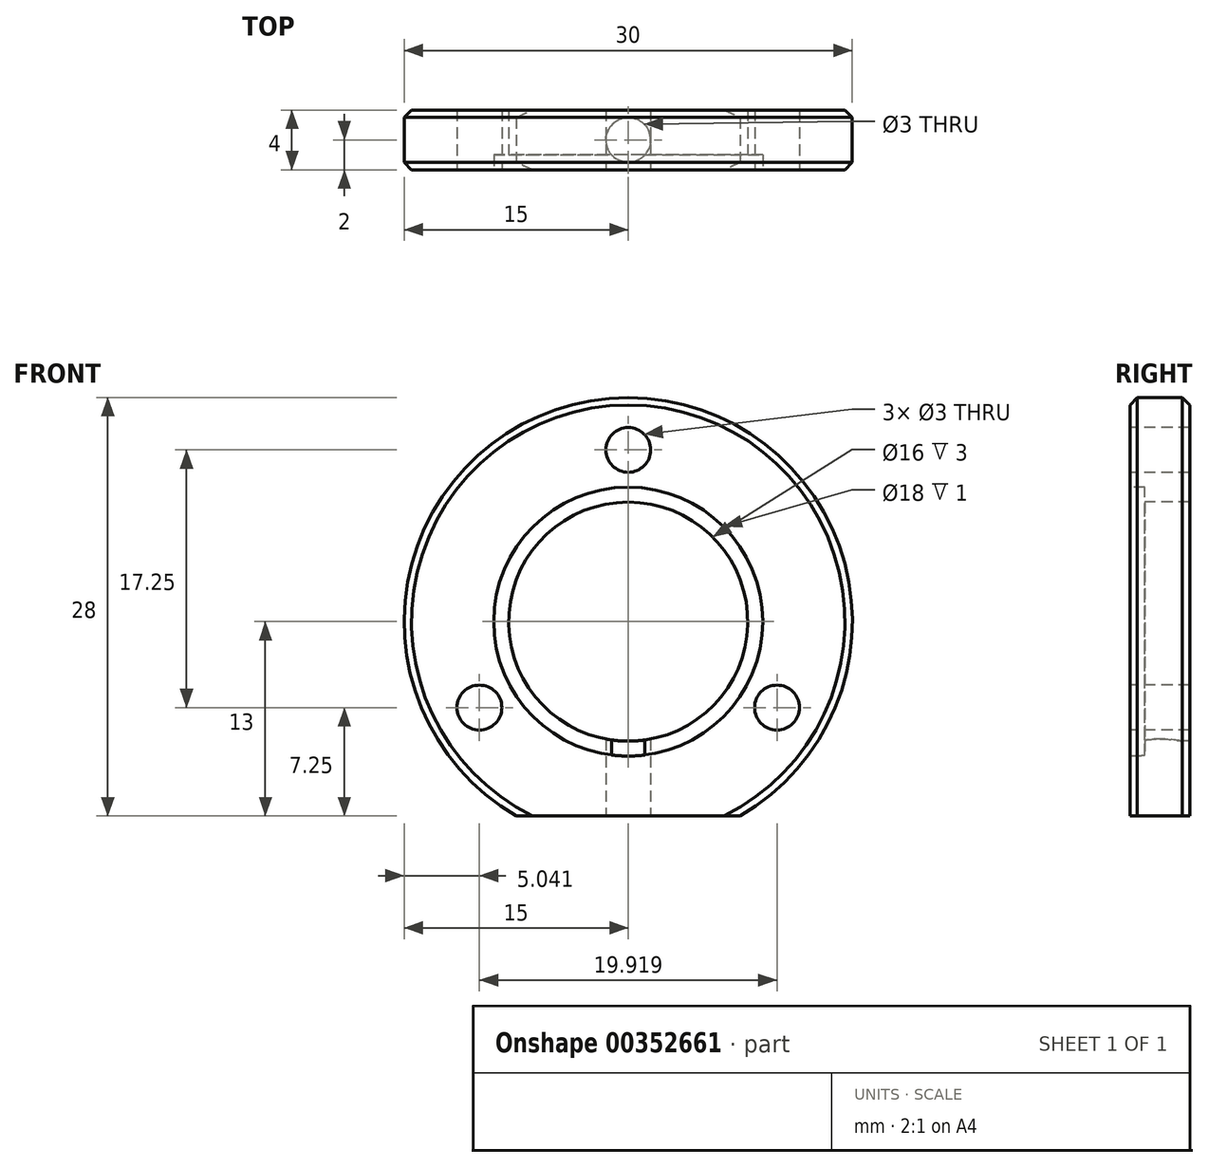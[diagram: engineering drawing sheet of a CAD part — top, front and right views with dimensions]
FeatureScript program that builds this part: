
annotation { "Feature Type Name" : "Feature", "Feature Type Description" : "" }
export const myFeature = defineFeature(function(context is Context, id is Id, definition is map)
    precondition{}
    {
        {
            var Q0;
            Q0=qCreatedBy(makeId("Right.planeOp"),FACE);
            var sketch = newSketch(context, id + "F0", { "sketchPlane" : qUnion([Q0])});
            skLineSegment(sketch, "E0", {"start": v(0, 0) * mm, "end": v(45.48, 0) * mm, "construction": true});
            skLineSegment(sketch, "E1", {"start": v(0, 8) * mm, "end": v(0, 9) * mm});
            skLineSegment(sketch, "E2", {"start": v(0, 9) * mm, "end": v(-1, 9) * mm});
            skLineSegment(sketch, "E3", {"start": v(-1, 9) * mm, "end": v(-1, 15) * mm});
            skLineSegment(sketch, "E4", {"start": v(-1, 15) * mm, "end": v(3, 15) * mm});
            skLineSegment(sketch, "E5", {"start": v(3, 15) * mm, "end": v(3, 8) * mm});
            skLineSegment(sketch, "E6", {"start": v(3, 8) * mm, "end": v(0, 8) * mm});
            skSolve(sketch);
        }
        {
            var Q0;
            Q0 = qSketchRegion(id + "F0", true);
            var Q1;
            Q1=sQuery(id+"F0.wireOp",EDGE,"E0");
            revolve(context, id + "F1", {"entities" : qUnion([Q0]), "axis" : qUnion([Q1]), "revolveType" : RevolveType.FULL});
        }
        {
            var Q0;
            Q0=makeQuery(id+"F1.opRevolve","SWEPT_EDGE",EDGE,{"disambiguationData":[OSD([sQuery(id+"F0.wireOp",EDGE,"E4"),sQuery(id+"F0.wireOp",EDGE,"E5")])]});
            var Q1;
            Q1=makeQuery(id+"F1.opRevolve","SWEPT_EDGE",EDGE,{"disambiguationData":[OSD([sQuery(id+"F0.wireOp",EDGE,"E3"),sQuery(id+"F0.wireOp",EDGE,"E4")])]});
            chamfer(context, id + "F2", {"entities" : qUnion([Q0, Q1]), "width" : .5 * mm, "tangentPropagation" : true});
        }
        {
            var Q0;
            Q0=makeQuery(id+"F1.opRevolve","SWEPT_FACE",FACE,{"disambiguationData":[OSD([sQuery(id+"F0.wireOp",EDGE,"E3")])]});
            var sketch = newSketch(context, id + "F3", { "sketchPlane" : qUnion([Q0])});
            skLineSegment(sketch, "E7.bottom", {"start": v(9, -13) * mm, "end": v(-9, -13) * mm});
            skLineSegment(sketch, "E7.top", {"start": v(9, -18) * mm, "end": v(-9, -18) * mm});
            skLineSegment(sketch, "E7.left", {"start": v(9, -13) * mm, "end": v(9, -18) * mm});
            skLineSegment(sketch, "E7.right", {"start": v(-9, -13) * mm, "end": v(-9, -18) * mm});
            skPoint(sketch, "E7.middle", {"position": v(0, -15.5) * mm});
            skSolve(sketch);
        }
        {
            var Q0;
            Q0 = qSketchRegion(id + "F3", true);
            extrude(context, id + "F4", {"entities" : qUnion([Q0]), "operationType" : NewBodyOperationType.REMOVE, "endBound" : BoundingType.THROUGH_ALL, "oppositeDirection" : true, "depth" : 25 * mm});
        }
        {
            var Q0;
            Q0=makeQuery(id+"F4.boolean.opBoolean","COPY",FACE,{"derivedFrom":makeQuery(id+"F4.opExtrude","SWEPT_FACE",FACE,{"disambiguationData":[OSD([sQuery(id+"F3.wireOp",EDGE,"E7.bottom")])]})});
            var sketch = newSketch(context, id + "F5", { "sketchPlane" : qUnion([Q0])});
            skCircle(sketch, "E8", {"center": v(0, -1) * mm, "radius": 1.5 * mm});
            skSolve(sketch);
        }
        {
            var Q0;
            Q0 = qSketchRegion(id + "F5", true);
            extrude(context, id + "F6", {"entities" : qUnion([Q0]), "operationType" : NewBodyOperationType.REMOVE, "endBound" : BoundingType.UP_TO_NEXT, "oppositeDirection" : true, "depth" : 4 * mm});
        }
        {
            var Q0;
            Q0=makeQuery(id+"F1.opRevolve","SWEPT_FACE",FACE,{"disambiguationData":[OSD([sQuery(id+"F0.wireOp",EDGE,"E3")])]});
            var sketch = newSketch(context, id + "F7", { "sketchPlane" : qUnion([Q0])});
            skCircle(sketch, "E9", {"center": v(0, 0) * mm, "radius": 11.5 * mm, "construction": true});
            skCircle(sketch, "E10", {"center": v(0, 11.5) * mm, "radius": 1.5 * mm});
            skPoint(sketch, "E10.centerSnap0", {"position": v(0, 14.5) * mm});
            skCircle(sketch, "E11.1.0", {"center": v(-9.96, -5.75) * mm, "radius": 1.5 * mm});
            skCircle(sketch, "E11.2.0", {"center": v(9.96, -5.75) * mm, "radius": 1.5 * mm});
            skSolve(sketch);
        }
        {
            var Q0;
            Q0 = qSketchRegion(id + "F7", true);
            extrude(context, id + "F8", {"entities" : qUnion([Q0]), "operationType" : NewBodyOperationType.REMOVE, "endBound" : BoundingType.THROUGH_ALL, "oppositeDirection" : true, "depth" : 25 * mm});
        }
    });
